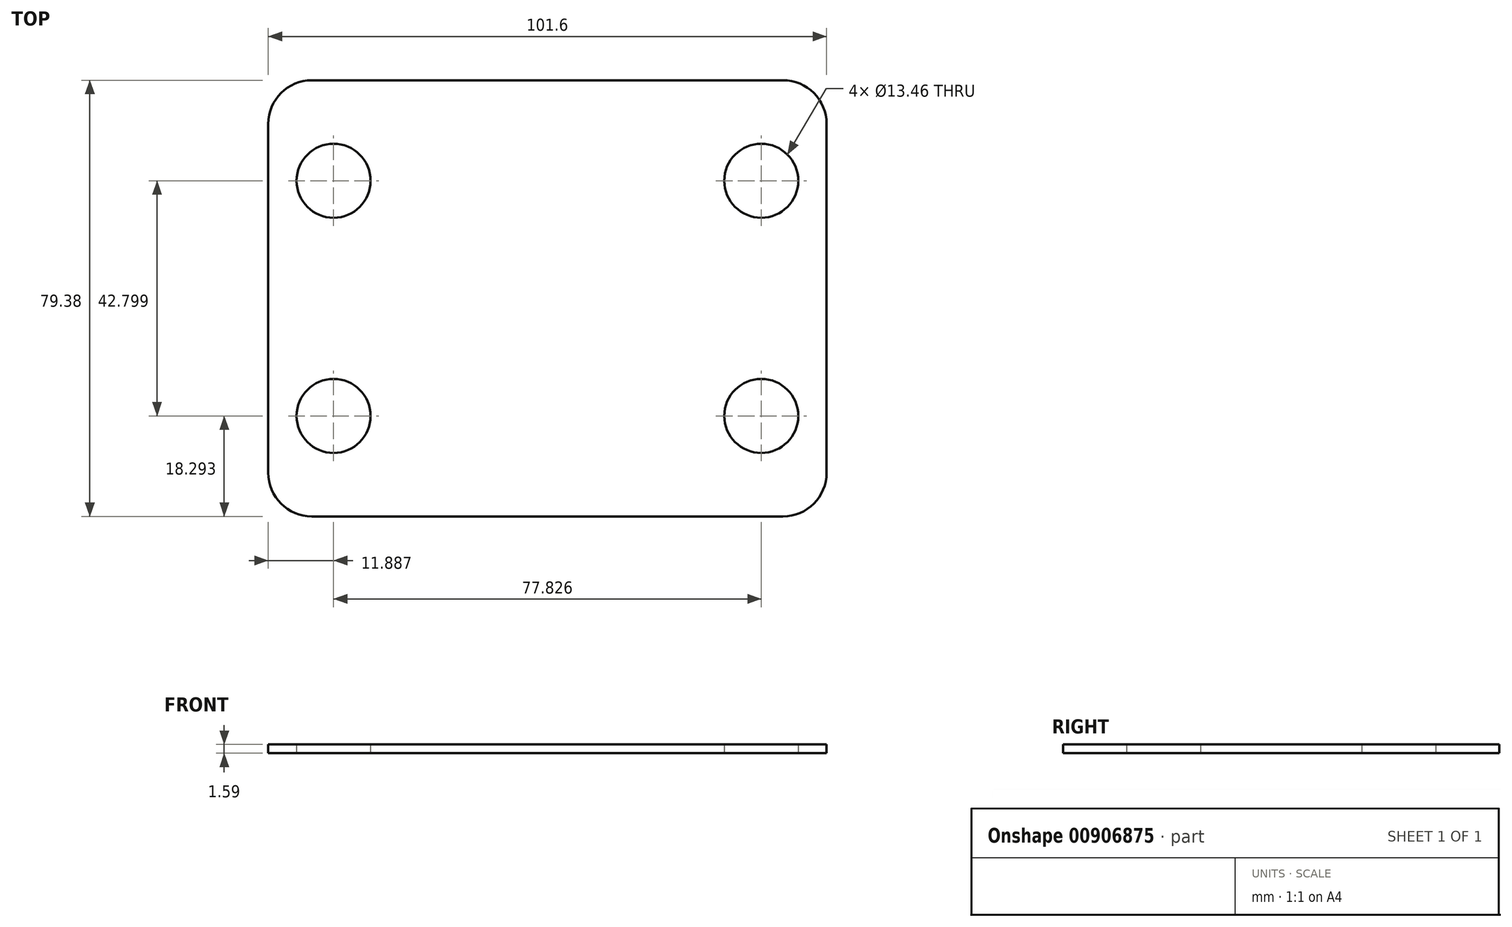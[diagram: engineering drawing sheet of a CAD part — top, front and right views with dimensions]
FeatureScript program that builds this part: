
annotation { "Feature Type Name" : "Feature", "Feature Type Description" : "" }
export const myFeature = defineFeature(function(context is Context, id is Id, definition is map)
    precondition{}
    {
        {
            var Q0;
            Q0=qCreatedBy(makeId("Top.planeOp"),FACE);
            var sketch = newSketch(context, id + "F0", { "sketchPlane" : qUnion([Q0])});
            skLineSegment(sketch, "E0.bottom", {"start": v(7.94, 0) * mm, "end": v(93.66, 0) * mm});
            skLineSegment(sketch, "E0.top", {"start": v(7.94, -79.38) * mm, "end": v(93.66, -79.38) * mm});
            skLineSegment(sketch, "E0.left", {"start": v(0, -7.94) * mm, "end": v(0, -71.44) * mm});
            skLineSegment(sketch, "E0.right", {"start": v(101.6, -7.94) * mm, "end": v(101.6, -71.44) * mm});
            skLineSegment(sketch, "E1", {"start": v(50.8, 0) * mm, "end": v(50.8, -79.38) * mm, "construction": true});
            skLineSegment(sketch, "E2", {"start": v(0, -39.69) * mm, "end": v(101.6, -39.69) * mm, "construction": true});
            skCircle(sketch, "E3", {"center": v(11.89, -18.29) * mm, "radius": 6.73 * mm});
            skCircle(sketch, "E4", {"center": v(89.71, -18.29) * mm, "radius": 6.73 * mm});
            skCircle(sketch, "E5", {"center": v(89.71, -61.09) * mm, "radius": 6.73 * mm});
            skCircle(sketch, "E6", {"center": v(11.89, -61.09) * mm, "radius": 6.73 * mm});
            skPoint(sketch, "E7.visualSharp", {"position": v(0, 0) * mm});
            skArc(sketch, "E7.filletArc", {"start": v(7.94, 0) * mm, "mid": v(2.32, -2.32) * mm, "end": v(0, -7.94) * mm});
            skPoint(sketch, "E8.visualSharp", {"position": v(101.6, 0) * mm});
            skArc(sketch, "E8.filletArc", {"start": v(101.6, -7.94) * mm, "mid": v(99.28, -2.32) * mm, "end": v(93.66, 0) * mm});
            skPoint(sketch, "E9.visualSharp", {"position": v(101.6, -79.38) * mm});
            skArc(sketch, "E9.filletArc", {"start": v(93.66, -79.38) * mm, "mid": v(99.28, -77.05) * mm, "end": v(101.6, -71.44) * mm});
            skPoint(sketch, "E10.visualSharp", {"position": v(0, -79.38) * mm});
            skArc(sketch, "E10.filletArc", {"start": v(0, -71.44) * mm, "mid": v(2.32, -77.05) * mm, "end": v(7.94, -79.38) * mm});
            skSolve(sketch);
        }
        {
            var Q0;
            Q0 = qSketchRegion(id + "F0", true);
            extrude(context, id + "F1", {"entities" : qUnion([Q0]), "depth" : 1.59 * mm, "offsetDistance" : 25.4 * mm});
        }
    });
